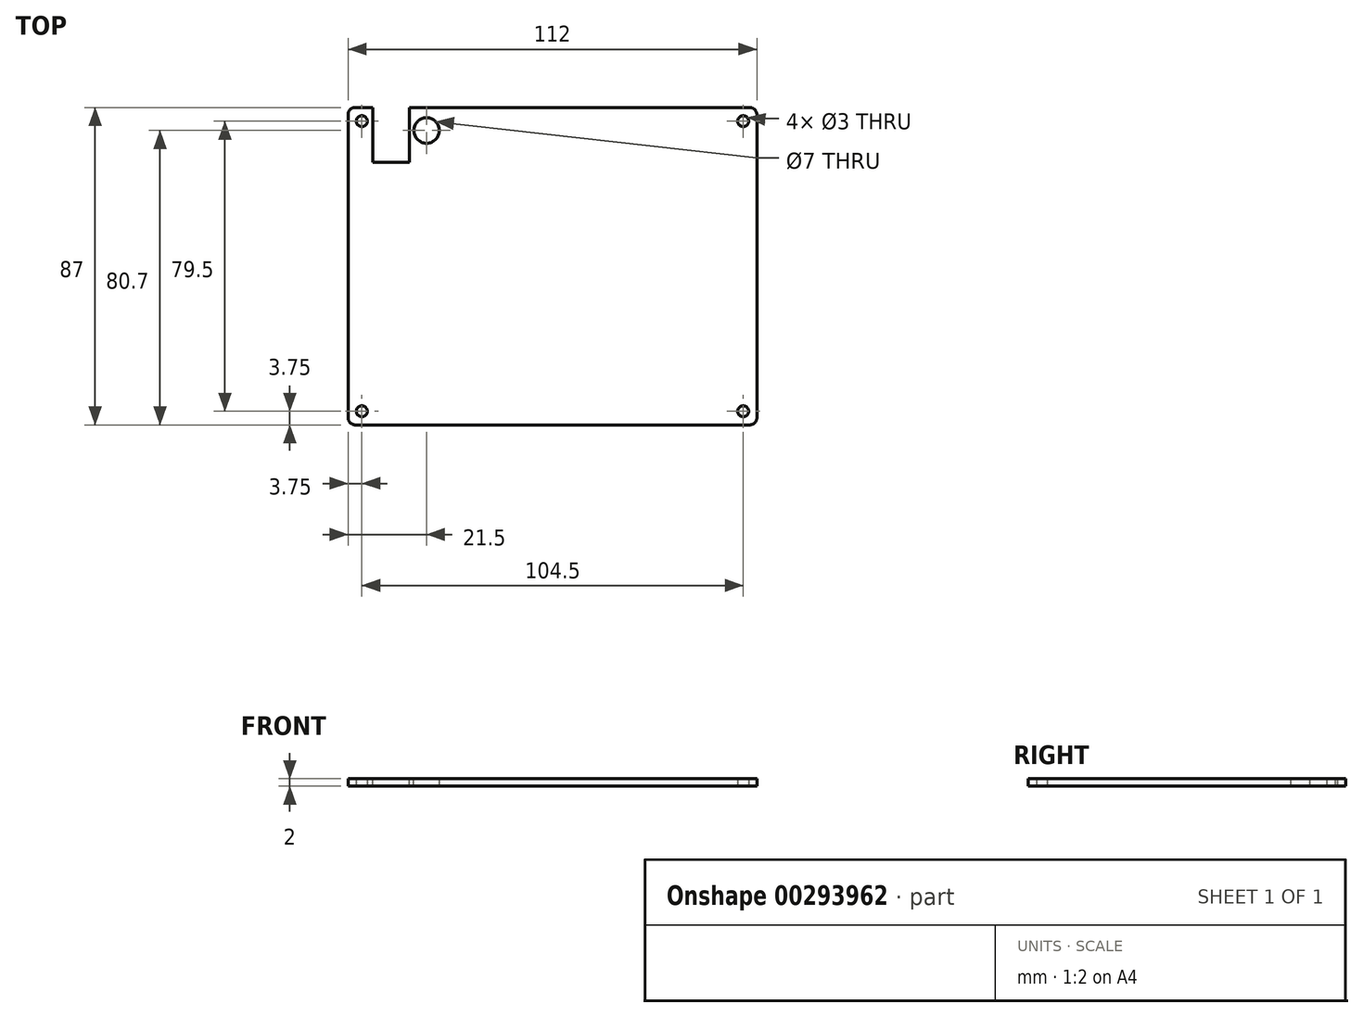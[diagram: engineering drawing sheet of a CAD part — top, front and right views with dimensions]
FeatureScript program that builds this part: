
annotation { "Feature Type Name" : "Feature", "Feature Type Description" : "" }
export const myFeature = defineFeature(function(context is Context, id is Id, definition is map)
    precondition{}
    {
        {
            var Q0;
            Q0=qCreatedBy(makeId("Top.planeOp"),FACE);
            var sketch = newSketch(context, id + "F0", { "sketchPlane" : qUnion([Q0])});
            skLineSegment(sketch, "E0.bottom", {"start": v(56, 43.5) * mm, "end": v(-56, 43.5) * mm});
            skLineSegment(sketch, "E0.top", {"start": v(56, -43.5) * mm, "end": v(-56, -43.5) * mm});
            skLineSegment(sketch, "E0.left", {"start": v(56, 43.5) * mm, "end": v(56, -43.5) * mm});
            skLineSegment(sketch, "E0.right", {"start": v(-56, 43.5) * mm, "end": v(-56, -43.5) * mm});
            skPoint(sketch, "E0.middle", {"position": v(0, 0) * mm});
            skCircle(sketch, "E1", {"center": v(-52.25, 39.75) * mm, "radius": 1.5 * mm});
            skCircle(sketch, "E2", {"center": v(-52.25, -39.75) * mm, "radius": 1.5 * mm});
            skCircle(sketch, "E3", {"center": v(52.25, -39.75) * mm, "radius": 1.5 * mm});
            skCircle(sketch, "E4", {"center": v(52.25, 39.75) * mm, "radius": 1.5 * mm});
            skSolve(sketch);
        }
        {
            var Q0;
            Q0=makeQuery(id+"F0.imprint","IMPRINT",FACE,{"disambiguationData":[TD([[makeQuery(id+"F0.imprint","IMPRINT",EDGE,{"derivedFrom":sQuery(id+"F0.wireOp",EDGE,"E0.bottom")}),1.0]])]});
            extrude(context, id + "F1", {"entities" : qUnion([Q0]), "depth" : 2 * mm});
        }
        {
            var Q0;
            Q0=makeQuery(id+"F1.opExtrude","SWEPT_EDGE",EDGE,{"disambiguationData":[OSD([sQuery(id+"F0.wireOp",EDGE,"E0.top"),sQuery(id+"F0.wireOp",EDGE,"E0.right")])]});
            var Q1;
            Q1=makeQuery(id+"F1.opExtrude","SWEPT_EDGE",EDGE,{"disambiguationData":[OSD([sQuery(id+"F0.wireOp",EDGE,"E0.bottom"),sQuery(id+"F0.wireOp",EDGE,"E0.right")])]});
            var Q2;
            Q2=makeQuery(id+"F1.opExtrude","SWEPT_EDGE",EDGE,{"disambiguationData":[OSD([sQuery(id+"F0.wireOp",EDGE,"E0.bottom"),sQuery(id+"F0.wireOp",EDGE,"E0.left")])]});
            var Q3;
            Q3=makeQuery(id+"F1.opExtrude","SWEPT_EDGE",EDGE,{"disambiguationData":[OSD([sQuery(id+"F0.wireOp",EDGE,"E0.top"),sQuery(id+"F0.wireOp",EDGE,"E0.left")])]});
            fillet(context, id + "F2", {"entities" : qUnion([Q0, Q1, Q2, Q3]), "radius" : 2 * mm, "tangentPropagation" : true, "allowEdgeOverflow" : false});
        }
        {
            var Q0;
            Q0=makeQuery(id+"F1.opExtrude","CAP_FACE",FACE,{"disambiguationData":[OSD([sQuery(id+"F0.wireOp",EDGE,"E0.bottom"),sQuery(id+"F0.wireOp",EDGE,"E0.top"),sQuery(id+"F0.wireOp",EDGE,"E0.left"),sQuery(id+"F0.wireOp",EDGE,"E0.right"),sQuery(id+"F0.wireOp",EDGE,"E1"),sQuery(id+"F0.wireOp",EDGE,"E2"),sQuery(id+"F0.wireOp",EDGE,"E3"),sQuery(id+"F0.wireOp",EDGE,"E4")])],"isStart":false});
            var sketch = newSketch(context, id + "F3", { "sketchPlane" : qUnion([Q0])});
            skLineSegment(sketch, "E5.bottom", {"start": v(-49.25, 43.5) * mm, "end": v(-39.25, 43.5) * mm});
            skLineSegment(sketch, "E5.top", {"start": v(-49.25, 28.5) * mm, "end": v(-39.25, 28.5) * mm});
            skLineSegment(sketch, "E5.left", {"start": v(-49.25, 43.5) * mm, "end": v(-49.25, 28.5) * mm});
            skLineSegment(sketch, "E5.right", {"start": v(-39.25, 43.5) * mm, "end": v(-39.25, 28.5) * mm});
            skCircle(sketch, "E6", {"center": v(-34.5, 37.2) * mm, "radius": 3.5 * mm});
            skSolve(sketch);
        }
        {
            var Q0;
            Q0=makeQuery(id+"F3.imprint","IMPRINT",FACE,{"disambiguationData":[TD([[makeQuery(id+"F3.imprint","IMPRINT",EDGE,{"derivedFrom":sQuery(id+"F3.wireOp",EDGE,"E5.bottom")}),1.0]])]});
            var Q1;
            Q1=makeQuery(id+"F3.imprint","IMPRINT",FACE,{"disambiguationData":[TD([[makeQuery(id+"F3.imprint","IMPRINT",EDGE,{"derivedFrom":sQuery(id+"F3.wireOp",EDGE,"E6")}),1.0]])]});
            extrude(context, id + "F4", {"entities" : qUnion([Q0, Q1]), "operationType" : NewBodyOperationType.REMOVE, "endBound" : BoundingType.THROUGH_ALL, "oppositeDirection" : true, "depth" : 25 * mm});
        }
    });
